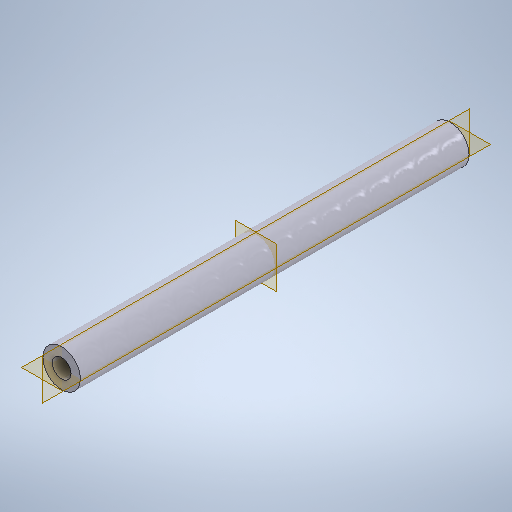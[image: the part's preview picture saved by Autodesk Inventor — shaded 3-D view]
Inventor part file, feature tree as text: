
AUTODESK INVENTOR PART (.ipt)
format: ipt  version: 2025.2 (Build 292293000, 293)  size: 248,832 bytes
history: native  units: mm
features: other x1, extrude x1, sketch x1
ambient origin geometry x8: Origin, YZ Plane, XZ Plane, XY Plane, X Axis, Y Axis, Z Axis, Center Point
bodies: Body1 (feature_tree)
feature tree (3):
  other  "Sólido1"
  extrude  "Extrusão1"  Depth=35.0mm
  sketch  "Esboço1"  dims[d0=70.0mm d1=35.0mm d2=725.0mm d3=0.0mm]
